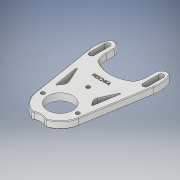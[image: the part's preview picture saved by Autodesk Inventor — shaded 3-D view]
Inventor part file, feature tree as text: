
AUTODESK INVENTOR PART (.ipt)
format: ipt  version: 2019.3 (Build 233278000, 278)  size: 648,192 bytes
history: native  units: mm
features: thread x3, emboss x2, fillet x2, sketch x2, extrude x1, chamfer x1, other x1
ambient origin geometry x8: Origin, YZ Plane, XZ Plane, XY Plane, X Axis, Y Axis, Z Axis, Center Point
bodies: Body1 (feature_tree)
feature tree (12):
  extrude  "Extrusion3"  Depth=20.0mm
  thread  "Thread1"  [1 undecoded]
  thread  "Thread2"  [1 undecoded]
  thread  "Thread3"  [1 undecoded]
  emboss  "Emboss1"
  emboss  "Emboss2"
  fillet  "Fillet3"  Radius=43.0mm
  fillet  "Fillet5"  Radius=3.5mm
  chamfer  "Chamfer3"  Distance=4.0mm
  other  "Center Lines"
  sketch  "Sketch1"  dims[d0=52.2mm d1=20.0mm d3=3.5mm d4=3.5mm d5=7.0mm d7=43.0mm d9=3.5mm]
  sketch  "Sketch3"  dims[d11=32.0mm d15=4.0mm d24=3.0mm d25=3.0mm d27=45.0deg d29=3.0mm d30=3.0mm d31=22.0mm d40=5.5mm d41=0.0mm d44=10.0mm d45=0.0mm d46=10.0mm d47=0.0mm d48=10.0mm d49=0.0mm d50=10.0mm d51=52.0mm d53=26.0mm d65=0.2mm d66=0.0mm d67=8.0mm d68=8.0mm d69=5.0mm d70=15.0mm d71=5.0mm d72=15.0mm d73=0.2mm d74=0.0mm d75=81.163203mm d76=7.5mm d77=3.75mm d81=6.25mm d82=12.5mm d85=5.0mm d86=4.0mm d91=0.5mm d94=2.0mm d95=0.5mm d96=2.0mm d97=45.0deg d98=15.0deg d99=24.0mm]
note: 3 required parameter values undecoded (feature->parameter linkage not recoverable at this tier; creation-order binding heuristic only, values carry confidence <= 0.55)
